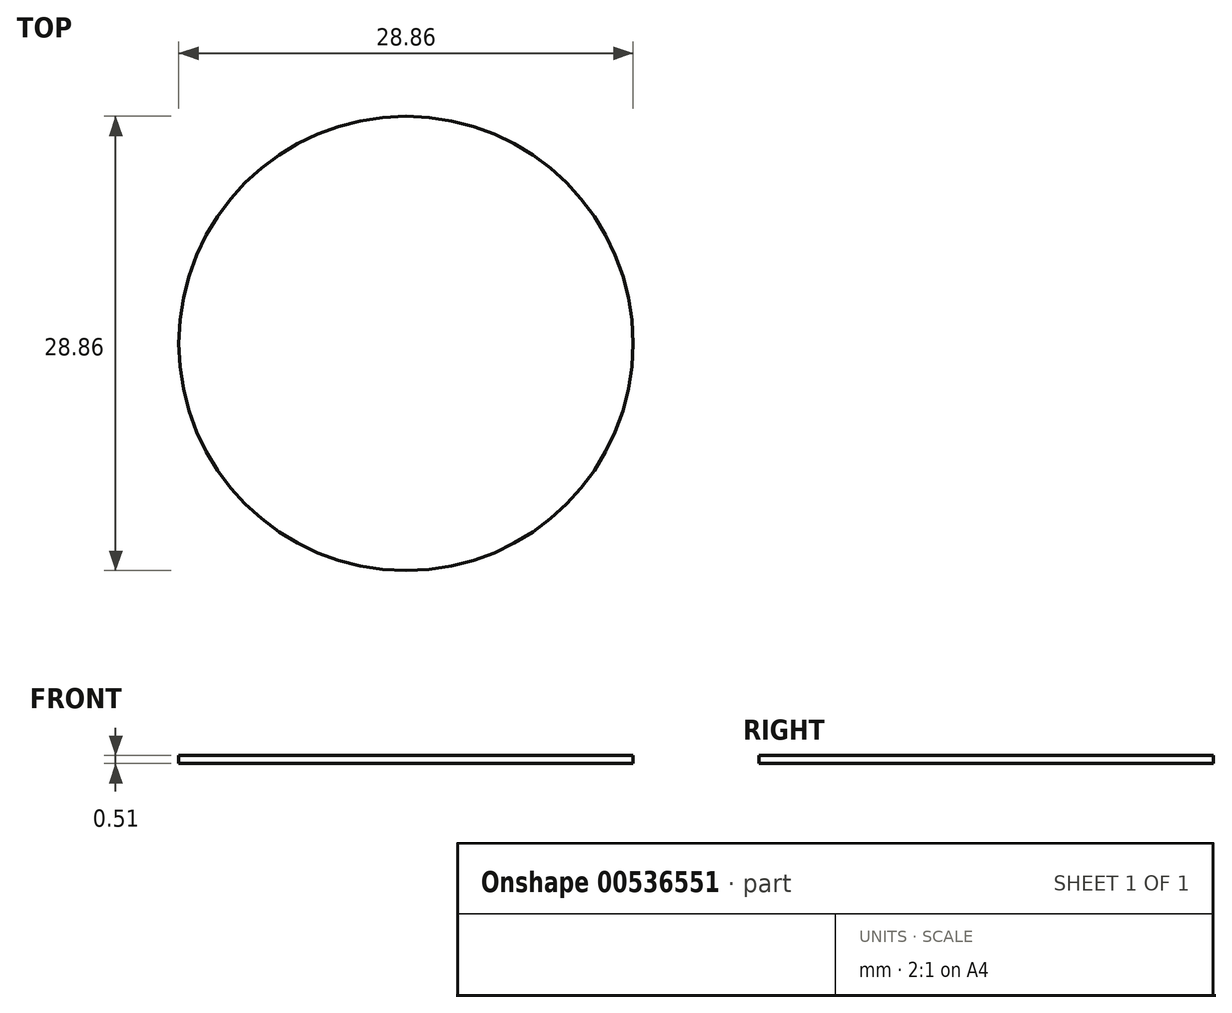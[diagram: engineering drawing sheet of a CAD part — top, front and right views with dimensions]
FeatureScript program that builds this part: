
annotation { "Feature Type Name" : "Feature", "Feature Type Description" : "" }
export const myFeature = defineFeature(function(context is Context, id is Id, definition is map)
    precondition{}
    {
        {
            var Q0;
            Q0=qCreatedBy(makeId("Top.planeOp"),FACE);
            var sketch = newSketch(context, id + "F0", { "sketchPlane" : qUnion([Q0])});
            skCircle(sketch, "E0", {"center": v(0, 0) * mm, "radius": 14.43 * mm});
            skSolve(sketch);
        }
        {
            var Q0;
            Q0 = qSketchRegion(id + "F0", true);
            extrude(context, id + "F1", {"entities" : qUnion([Q0]), "depth" : 0.5 * mm, "offsetDistance" : 25.4 * mm});
        }
    });
